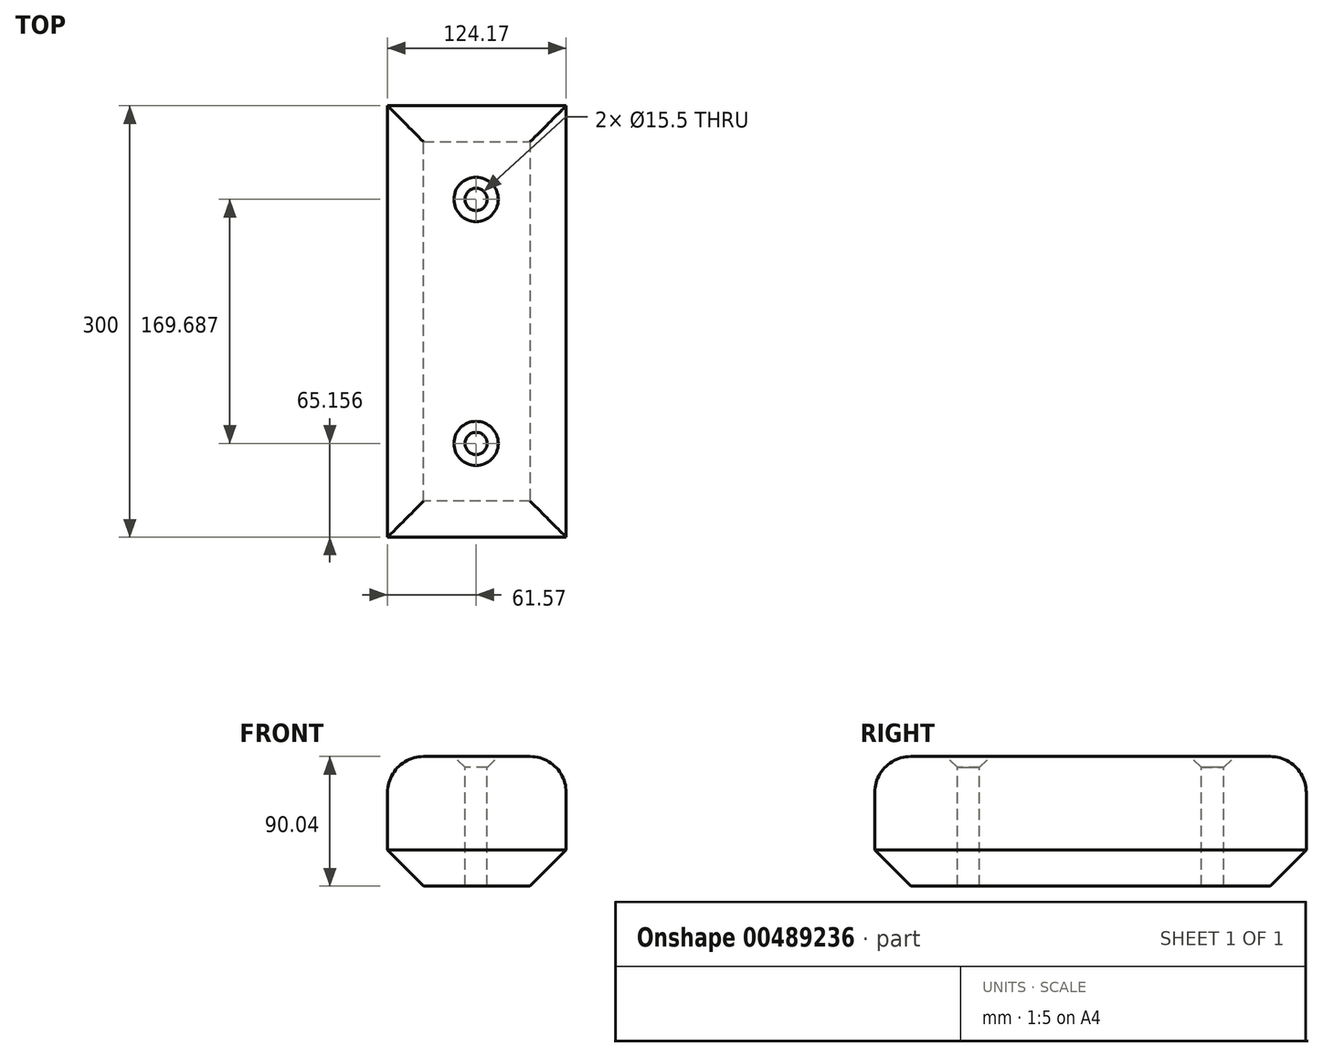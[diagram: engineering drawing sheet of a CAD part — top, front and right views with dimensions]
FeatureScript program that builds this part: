
annotation { "Feature Type Name" : "Feature", "Feature Type Description" : "" }
export const myFeature = defineFeature(function(context is Context, id is Id, definition is map)
    precondition{}
    {
        {
            var Q0;
            Q0=qCreatedBy(makeId("Front.planeOp"),FACE);
            var sketch = newSketch(context, id + "F0", { "sketchPlane" : qUnion([Q0])});
            skLineSegment(sketch, "E0.bottom", {"start": v(-61.57, 62.54) * mm, "end": v(62.6, 62.54) * mm});
            skLineSegment(sketch, "E0.top", {"start": v(-61.57, -27.5) * mm, "end": v(62.6, -27.5) * mm});
            skLineSegment(sketch, "E0.left", {"start": v(-61.57, 62.54) * mm, "end": v(-61.57, -27.5) * mm});
            skLineSegment(sketch, "E0.right", {"start": v(62.6, 62.54) * mm, "end": v(62.6, -27.5) * mm});
            skSolve(sketch);
        }
        {
            var Q0;
            Q0 = qSketchRegion(id + "F0", true);
            extrude(context, id + "F1", {"entities" : qUnion([Q0]), "depth" : 150 * mm});
        }
        {
            var Q0;
            Q0=makeQuery(id+"F1.opExtrude","CAP_EDGE",EDGE,{"disambiguationData":[OSD([sQuery(id+"F0.wireOp",EDGE,"E0.bottom")])],"isStart":false});
            var Q1;
            Q1=makeQuery(id+"F1.opExtrude","SWEPT_EDGE",EDGE,{"disambiguationData":[OSD([sQuery(id+"F0.wireOp",EDGE,"E0.bottom"),sQuery(id+"F0.wireOp",EDGE,"E0.right")])]});
            var Q2;
            Q2=makeQuery(id+"F1.opExtrude","SWEPT_EDGE",EDGE,{"disambiguationData":[OSD([sQuery(id+"F0.wireOp",EDGE,"E0.bottom"),sQuery(id+"F0.wireOp",EDGE,"E0.left")])]});
            fillet(context, id + "F2", {"entities" : qUnion([Q0, Q1, Q2]), "radius" : 25 * mm, "tangentPropagation" : true, "allowEdgeOverflow" : false});
        }
        {
            var Q0;
            Q0=makeQuery(id+"F1.opExtrude","SWEPT_FACE",FACE,{"disambiguationData":[OSD([sQuery(id+"F0.wireOp",EDGE,"E0.bottom")])]});
            var sketch = newSketch(context, id + "F3", { "sketchPlane" : qUnion([Q0])});
            skPoint(sketch, "E1", {"position": v(0, -84.84) * mm});
            skSolve(sketch);
        }
        {
            var Q0;
            Q0=sQuery(id+"F3.wireOp",VERTEX,"E1");
            var Q1;
            Q1=makeQuery(id+"F1.opExtrude","SWEPT_BODY",BODY,{"disambiguationData":[OSD([sQuery(id+"F0.wireOp",EDGE,"E0.bottom"),sQuery(id+"F0.wireOp",EDGE,"E0.top"),sQuery(id+"F0.wireOp",EDGE,"E0.left"),sQuery(id+"F0.wireOp",EDGE,"E0.right")])]});
            hole(context, id + "F4", {"style" : HoleStyle.C_SINK, "endStyle" : HoleEndStyle.THROUGH, "standardTappedOrClearance" : lookupTablePath({ "standard" : "ISO", "fit" : "Normal", "size" : "M14", "type" : "Clearance" }), "standardBlindInLast" : lookupTablePath({ "fit" : "Standard", "standard" : "ISO", "size" : "M14", "type" : "Clearance" }), "holeDiameter" : 15.5 * mm, "cSinkDiameter" : 30.8 * mm, "cSinkAngle" : 90 * degree, "isTappedThrough" : true, "tappedDepth" : 12 * mm, "tapClearance" : 3, "locations" : qUnion([Q0]), "scope" : qUnion([Q1])});
        }
        {
            var Q0;
            Q0=makeQuery(id+"F1.opExtrude","SWEPT_BODY",BODY,{"disambiguationData":[OSD([sQuery(id+"F0.wireOp",EDGE,"E0.bottom"),sQuery(id+"F0.wireOp",EDGE,"E0.top"),sQuery(id+"F0.wireOp",EDGE,"E0.left"),sQuery(id+"F0.wireOp",EDGE,"E0.right")])]});
            var Q1;
            Q1=qCreatedBy(makeId("Front.planeOp"),FACE);
            mirror(context, id + "F5", {"operationType" : NewBodyOperationType.ADD, "entities" : qUnion([Q0]), "mirrorPlane" : qUnion([Q1])});
        }
        {
            var Q0;
            {var subQ0=makeQuery(id+"F1.opExtrude","SWEPT_EDGE",EDGE,{"disambiguationData":[OSD([sQuery(id+"F0.wireOp",EDGE,"E0.top"),sQuery(id+"F0.wireOp",EDGE,"E0.right")])]});Q0=makeQuery(id+"F5.boolean.opBoolean","MERGE",EDGE,{"derivedFrom":[subQ0,makeQuery(id+"F5.opPattern","COPY",EDGE,{"derivedFrom":subQ0,"instanceName":"1"})]});}
            var Q1;
            Q1=makeQuery(id+"F5.opPattern","COPY",EDGE,{"derivedFrom":makeQuery(id+"F1.opExtrude","CAP_EDGE",EDGE,{"disambiguationData":[OSD([sQuery(id+"F0.wireOp",EDGE,"E0.top")])],"isStart":false}),"instanceName":"1"});
            var Q2;
            Q2=makeQuery(id+"F1.opExtrude","CAP_EDGE",EDGE,{"disambiguationData":[OSD([sQuery(id+"F0.wireOp",EDGE,"E0.top")])],"isStart":false});
            var Q3;
            {var subQ0=makeQuery(id+"F1.opExtrude","SWEPT_EDGE",EDGE,{"disambiguationData":[OSD([sQuery(id+"F0.wireOp",EDGE,"E0.top"),sQuery(id+"F0.wireOp",EDGE,"E0.left")])]});Q3=makeQuery(id+"F5.boolean.opBoolean","MERGE",EDGE,{"derivedFrom":[subQ0,makeQuery(id+"F5.opPattern","COPY",EDGE,{"derivedFrom":subQ0,"instanceName":"1"})]});}
            chamfer(context, id + "F6", {"entities" : qUnion([Q0, Q1, Q2, Q3]), "width" : 25 * mm, "tangentPropagation" : true});
        }
    });
